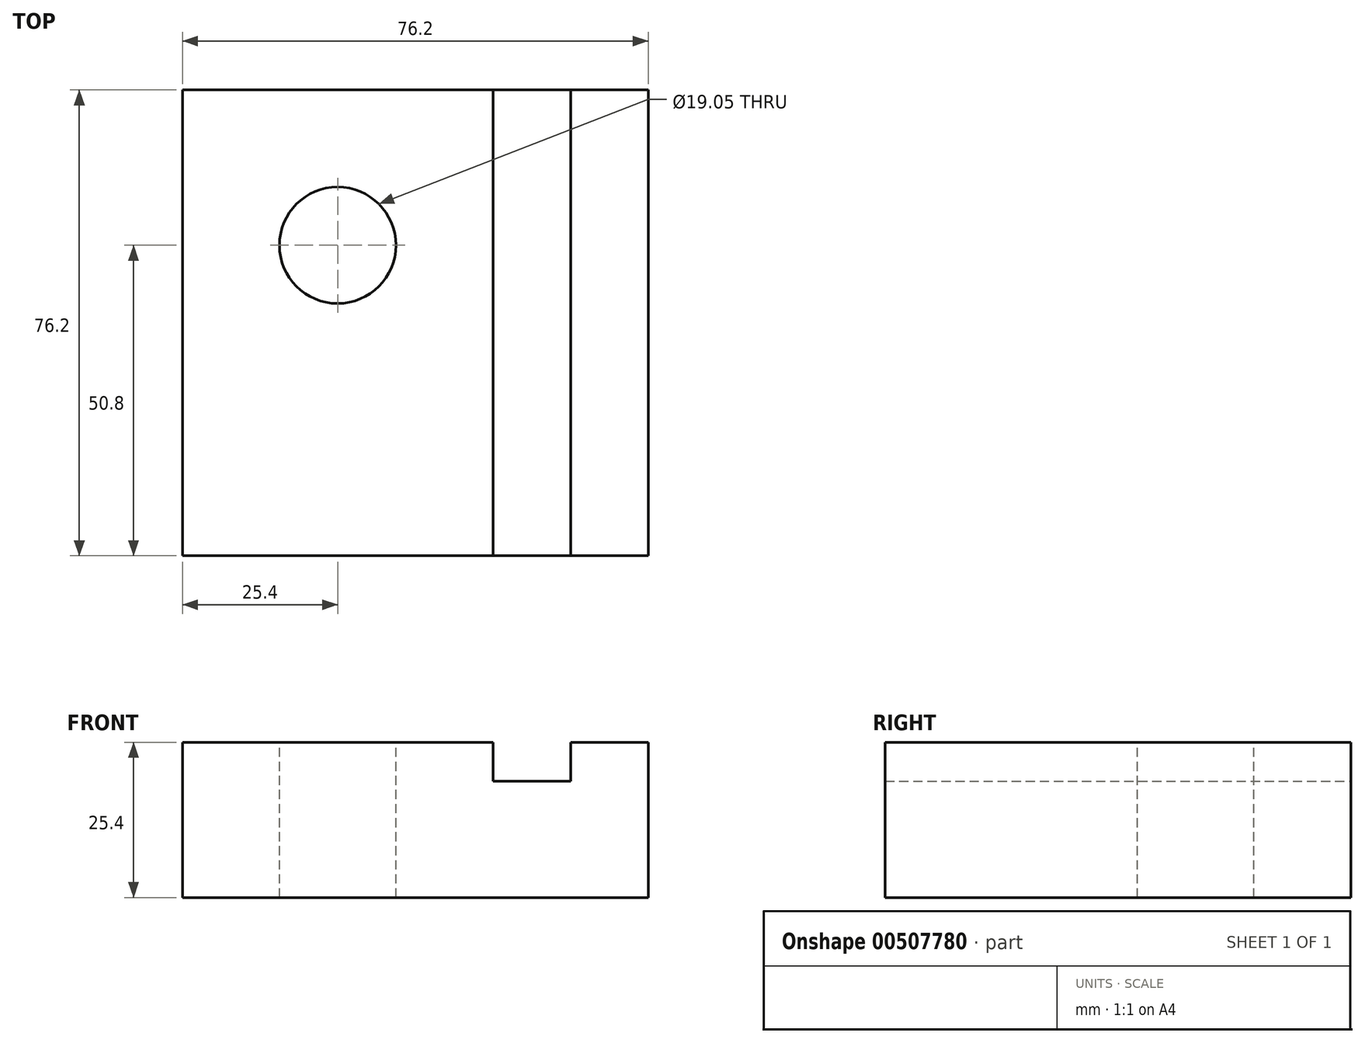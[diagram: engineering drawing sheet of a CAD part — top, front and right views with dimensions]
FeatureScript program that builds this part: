
annotation { "Feature Type Name" : "Feature", "Feature Type Description" : "" }
export const myFeature = defineFeature(function(context is Context, id is Id, definition is map)
    precondition{}
    {
        {
            var Q0;
            Q0=qCreatedBy(makeId("Front.planeOp"),FACE);
            var sketch = newSketch(context, id + "F0", { "sketchPlane" : qUnion([Q0])});
            skLineSegment(sketch, "E0", {"start": v(0, 25.4) * mm, "end": v(0, 0) * mm});
            skLineSegment(sketch, "E1", {"start": v(0, 25.4) * mm, "end": v(50.8, 25.4) * mm});
            skLineSegment(sketch, "E2", {"start": v(50.8, 25.4) * mm, "end": v(50.8, 19.05) * mm});
            skLineSegment(sketch, "E3", {"start": v(50.8, 19.05) * mm, "end": v(63.5, 19.05) * mm});
            skLineSegment(sketch, "E4", {"start": v(63.5, 19.05) * mm, "end": v(63.5, 25.4) * mm});
            skLineSegment(sketch, "E5", {"start": v(63.5, 25.4) * mm, "end": v(76.2, 25.4) * mm});
            skLineSegment(sketch, "E6", {"start": v(76.2, 25.4) * mm, "end": v(76.2, 0) * mm});
            skLineSegment(sketch, "E7", {"start": v(76.2, 0) * mm, "end": v(0, 0) * mm});
            skSolve(sketch);
        }
        {
            var Q0;
            Q0=makeQuery(id+"F0.imprint","IMPRINT",FACE,{"disambiguationData":[TD([[makeQuery(id+"F0.imprint","IMPRINT",EDGE,{"derivedFrom":sQuery(id+"F0.wireOp",EDGE,"E0")}),1.0]])]});
            extrude(context, id + "F1", {"entities" : qUnion([Q0]), "depth" : 76.2 * mm});
        }
        {
            var Q0;
            Q0=makeQuery(id+"F1.opExtrude","SWEPT_FACE",FACE,{"disambiguationData":[OSD([sQuery(id+"F0.wireOp",EDGE,"E1")])]});
            var sketch = newSketch(context, id + "F2", { "sketchPlane" : qUnion([Q0])});
            skLineSegment(sketch, "E8", {"start": v(0, 0) * mm, "end": v(25.4, 0) * mm, "construction": true});
            skLineSegment(sketch, "E9", {"start": v(25.4, 0) * mm, "end": v(25.4, -25.4) * mm, "construction": true});
            skCircle(sketch, "E10", {"center": v(25.4, -25.4) * mm, "radius": 9.53 * mm});
            skSolve(sketch);
        }
        {
            var Q0;
            Q0=makeQuery(id+"F2.imprint","IMPRINT",FACE,{"disambiguationData":[TD([[makeQuery(id+"F2.imprint","IMPRINT",EDGE,{"derivedFrom":sQuery(id+"F2.wireOp",EDGE,"E10")}),1.0]])]});
            extrude(context, id + "F3", {"entities" : qUnion([Q0]), "operationType" : NewBodyOperationType.REMOVE, "endBound" : BoundingType.THROUGH_ALL, "oppositeDirection" : true, "depth" : 25.4 * mm});
        }
    });
